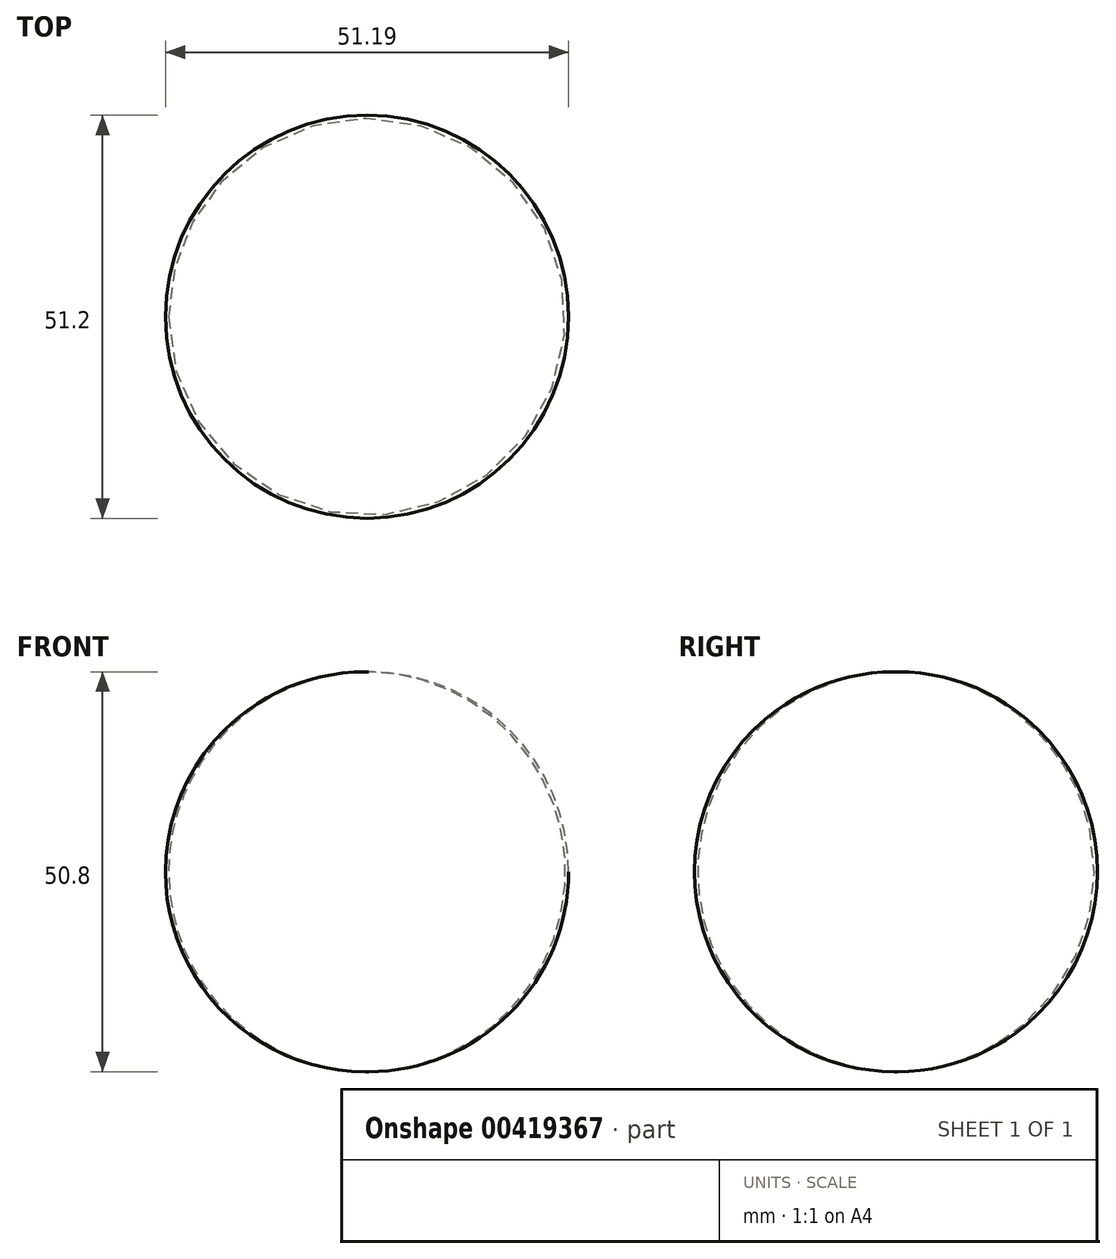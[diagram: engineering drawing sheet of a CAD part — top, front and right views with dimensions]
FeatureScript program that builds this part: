
annotation { "Feature Type Name" : "Feature", "Feature Type Description" : "" }
export const myFeature = defineFeature(function(context is Context, id is Id, definition is map)
    precondition{}
    {
        {
            var Q0;
            Q0=qCreatedBy(makeId("Front.planeOp"),FACE);
            var sketch = newSketch(context, id + "F0", { "sketchPlane" : qUnion([Q0])});
            skArc(sketch, "E0", {"start": v(-12.6, 45.07) * mm, "mid": v(-38.2, 19.67) * mm, "end": v(-12.6, -5.73) * mm});
            skLineSegment(sketch, "E1", {"start": v(-12.6, 45.07) * mm, "end": v(-12.6, -8.78) * mm});
            skSolve(sketch);
        }
        {
            var Q0;
            {var subQ0=sQuery(id+"F0.wireOp",EDGE,"E0");Q0=makeQuery(id+"F0.imprint","IMPRINT",FACE,{"disambiguationData":[TD([[makeQuery(id+"F0.imprint","IMPRINT",EDGE,{"derivedFrom":subQ0}),1.0]])]});}
            var Q1;
            Q1=sQuery(id+"F0.wireOp",EDGE,"E1");
            revolve(context, id + "F1", {"entities" : qUnion([Q0]), "axis" : qUnion([Q1]), "revolveType" : RevolveType.FULL});
        }
    });
